# Revit family: 206_Water battery-_
name_source: partatom
category: Duct Accessories
revit_build: Autodesk Revit 2018 (Build: 20170223_1515(x64)
units: mm (PartAtom-declared; Revit-internal decimal feet)

## family parameters
Always vertical = Yes
Cut with Voids When Loaded = No
Part Type = Breaks Into
Round Connector Dimension = Use Diameter
Shared = No
Work Plane-Based = No

## types (5) — shared parameters
CAT0 = Yes
Description = Water coil complete
H2D = 205 mm  [stored 0.672572 ft]
L2D = 350 mm  [stored 1.14829 ft]
Manufacturer = Flexit
QmdConnectorList = 201;D;202;D
W2D = 204 mm  [stored 0.669291 ft]
X1 = 175 mm  [stored 0.574147 ft]
magiPartTypeId = 206
magiProductFamilyId = Water battery-*

## per-type parameters (varying)
| type | CH | D | Y1 | Y1__ve | Z1 | magiProductId |
| 160-112667 | 205 mm  [stored 0.672572 ft] | 160 mm | 102 mm  [stored 0.334646 ft] | -102 mm  [stored -0.334646 ft] | 103 mm | Water battery-160-A |
| 160-112668 | 205 mm  [stored 0.672572 ft] | 160 mm | 102 mm  [stored 0.334646 ft] | -102 mm  [stored -0.334646 ft] | 103 mm | Water battery-160-B |
| 160-112669 | 205 mm  [stored 0.672572 ft] | 160 mm | 102 mm  [stored 0.334646 ft] | -102 mm  [stored -0.334646 ft] | 103 mm | Water battery-160-C |
| 200-112670 | 255 mm  [stored 0.836614 ft] | 200 mm | 176 mm | -176 mm | 128 mm | Water battery-200-A |
| 200-112671 | 255 mm  [stored 0.836614 ft] | 200 mm | 176 mm | -176 mm | 128 mm | Water battery-200-B |

note: column(s) folded — value = type name in every type: MC Product Code

note: [stored X ft] marks values corroborated as IEEE doubles in the binary element streams (Revit-internal decimal feet)

## geometry (parser evidence)
native form markers: Sweep x2
no freeform markers — native parametric forms only
